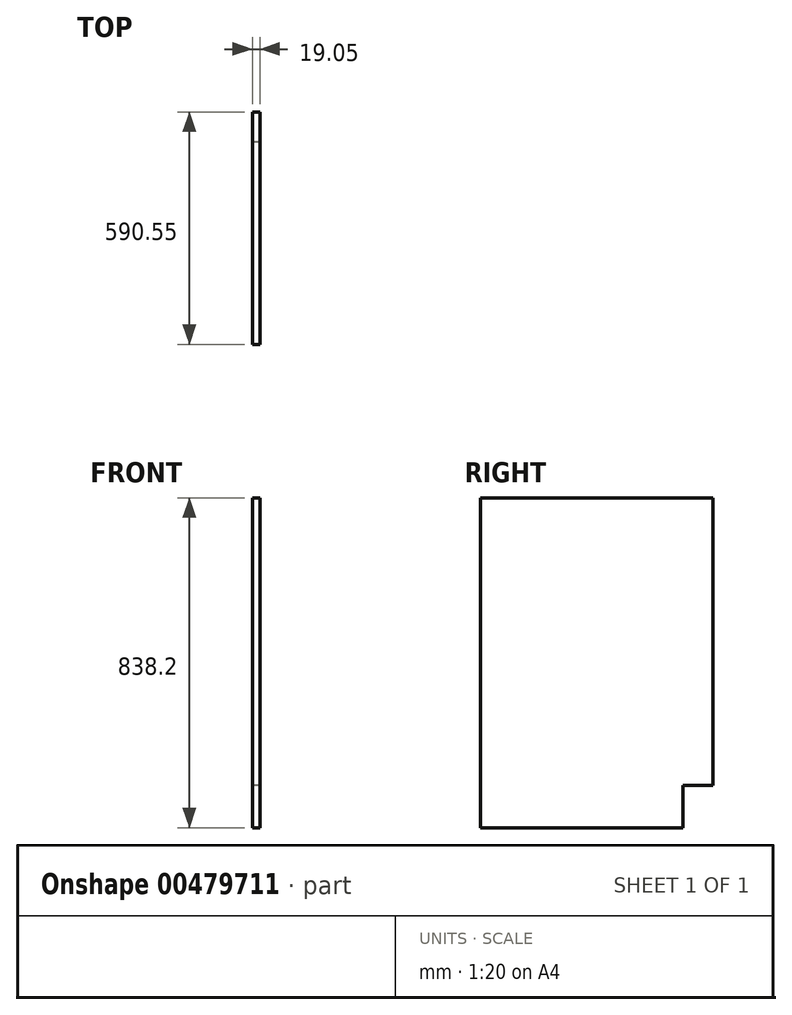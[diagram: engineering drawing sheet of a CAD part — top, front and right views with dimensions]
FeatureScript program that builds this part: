
annotation { "Feature Type Name" : "Feature", "Feature Type Description" : "" }
export const myFeature = defineFeature(function(context is Context, id is Id, definition is map)
    precondition{}
    {
        {
            var Q0;
            Q0=qCreatedBy(makeId("Right.planeOp"),FACE);
            var sketch = newSketch(context, id + "F0", { "sketchPlane" : qUnion([Q0])});
            skLineSegment(sketch, "E0.bottom", {"start": v(0, 0) * mm, "end": v(514.35, 0) * mm});
            skLineSegment(sketch, "E0.top", {"start": v(0, 838.2) * mm, "end": v(590.55, 838.2) * mm});
            skLineSegment(sketch, "E0.left", {"start": v(0, 0) * mm, "end": v(0, 838.2) * mm});
            skLineSegment(sketch, "E0.right", {"start": v(590.55, 107.95) * mm, "end": v(590.55, 838.2) * mm});
            skLineSegment(sketch, "E1", {"start": v(590.55, 107.95) * mm, "end": v(514.35, 107.95) * mm});
            skLineSegment(sketch, "E2", {"start": v(514.35, 107.95) * mm, "end": v(514.35, 0) * mm});
            skSolve(sketch);
        }
        {
            var Q0;
            Q0=qSketchRegion(id+"F0",true);
            extrude(context, id + "F1", {"entities" : qUnion([Q0]), "depth" : 19.05 * mm});
        }
    });
